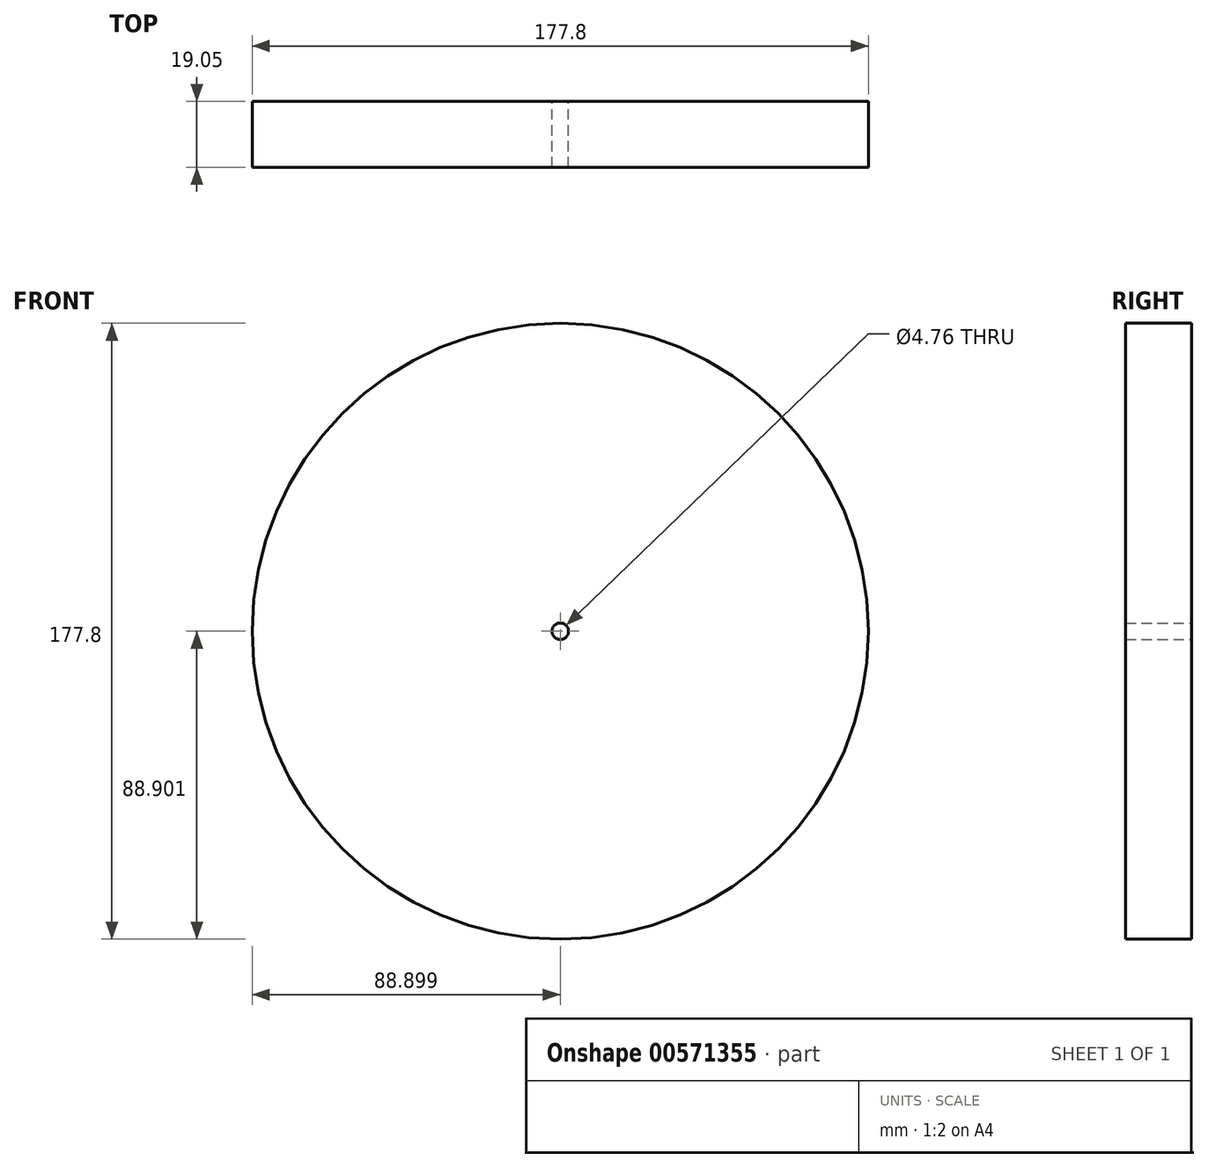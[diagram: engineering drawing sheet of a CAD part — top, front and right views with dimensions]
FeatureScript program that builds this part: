
annotation { "Feature Type Name" : "Feature", "Feature Type Description" : "" }
export const myFeature = defineFeature(function(context is Context, id is Id, definition is map)
    precondition{}
    {
        {
            var Q0;
            Q0=qCreatedBy(makeId("Front.planeOp"),FACE);
            var sketch = newSketch(context, id + "F0", { "sketchPlane" : qUnion([Q0])});
            skCircle(sketch, "E0", {"center": v(-37.12, 18.42) * mm, "radius": 88.9 * mm});
            skCircle(sketch, "E1", {"center": v(-37.12, 18.42) * mm, "radius": 2.38 * mm});
            skSolve(sketch);
        }
        {
            var Q0;
            Q0=makeQuery(id+"F0.imprint","IMPRINT",FACE,{"disambiguationData":[TD([[makeQuery(id+"F0.imprint","IMPRINT",EDGE,{"derivedFrom":sQuery(id+"F0.wireOp",EDGE,"E0")}),1.0]])]});
            extrude(context, id + "F1", {"entities" : qUnion([Q0]), "depth" : 19.05 * mm, "offsetDistance" : 25.4 * mm});
        }
    });
